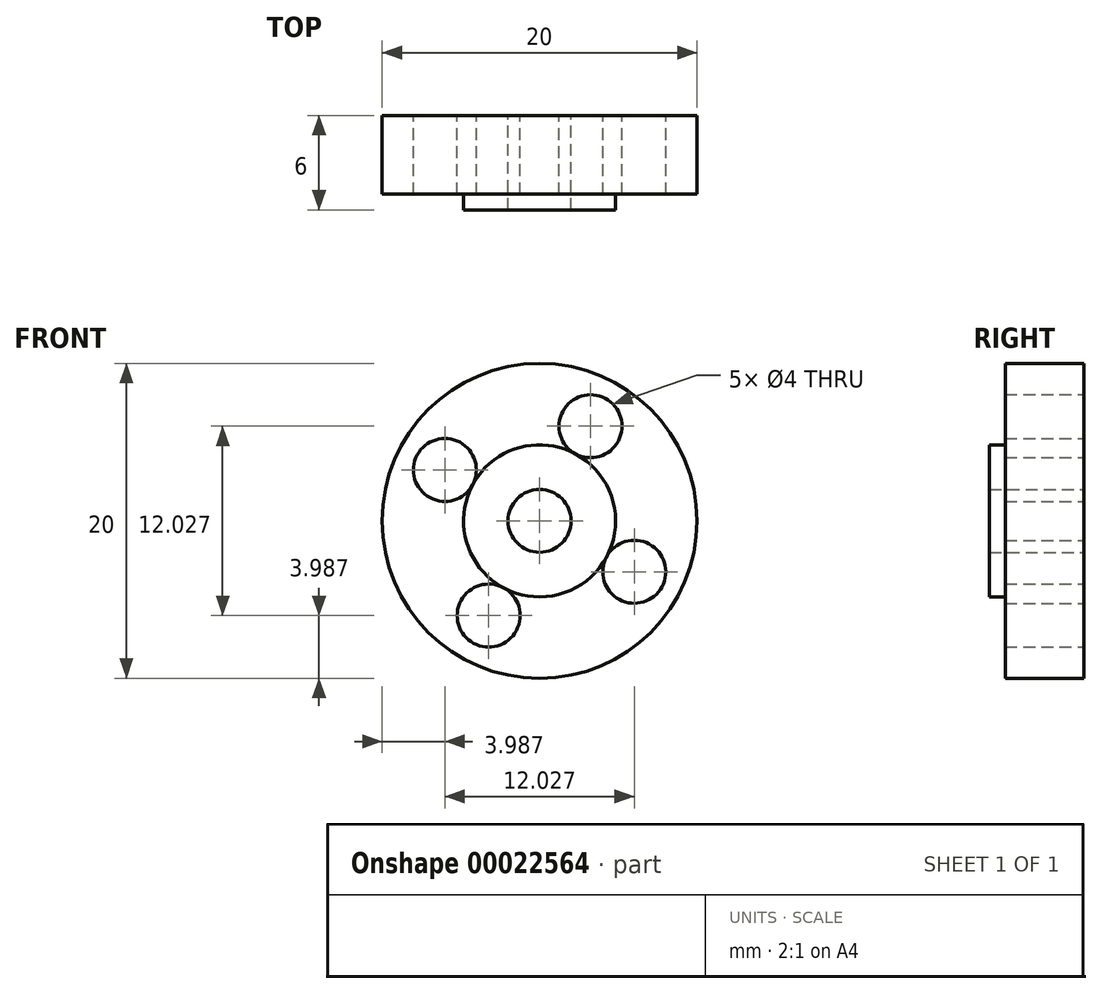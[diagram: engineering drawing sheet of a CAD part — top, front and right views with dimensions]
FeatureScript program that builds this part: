
annotation { "Feature Type Name" : "Feature", "Feature Type Description" : "" }
export const myFeature = defineFeature(function(context is Context, id is Id, definition is map)
    precondition{}
    {
        {
            var Q0;
            Q0=qCreatedBy(makeId("Front.planeOp"),FACE);
            var sketch = newSketch(context, id + "F0", { "sketchPlane" : qUnion([Q0])});
            skCircle(sketch, "E0", {"center": v(0, 0) * mm, "radius": 10 * mm});
            skCircle(sketch, "E1", {"center": v(0, 0) * mm, "radius": 2 * mm});
            skCircle(sketch, "E2", {"center": v(0, 0) * mm, "radius": 4.83 * mm});
            skCircle(sketch, "E3.cCircle", {"center": v(0, 0) * mm, "radius": 4.83 * mm, "construction": true});
            skLineSegment(sketch, "E3.0", {"start": v(6.01, -3.24) * mm, "end": v(-3.24, -6.01) * mm});
            skLineSegment(sketch, "E3.1", {"start": v(-3.24, -6.01) * mm, "end": v(-6.01, 3.24) * mm});
            skLineSegment(sketch, "E3.2", {"start": v(-6.01, 3.24) * mm, "end": v(3.24, 6.01) * mm});
            skLineSegment(sketch, "E3.3", {"start": v(3.24, 6.01) * mm, "end": v(6.01, -3.24) * mm});
            skPoint(sketch, "E3.0.midPoint", {"position": v(1.39, -4.62) * mm});
            skCircle(sketch, "E4", {"center": v(-3.24, -6.01) * mm, "radius": 2 * mm});
            skCircle(sketch, "E5", {"center": v(6.01, -3.24) * mm, "radius": 2 * mm});
            skCircle(sketch, "E6", {"center": v(3.24, 6.01) * mm, "radius": 2 * mm});
            skCircle(sketch, "E7", {"center": v(-6.01, 3.24) * mm, "radius": 2 * mm});
            skSolve(sketch);
        }
        {
            var Q0;
            Q0=makeQuery(id+"F0.imprint","IMPRINT",FACE,{"disambiguationData":[TD([[makeQuery(id+"F0.imprint","IMPRINT",EDGE,{"derivedFrom":sQuery(id+"F0.wireOp",EDGE,"E1")}),-1.0]])]});
            var Q1;
            Q1=makeQuery(id+"F0.imprint","IMPRINT",FACE,{"disambiguationData":[TD([[makeQuery(id+"F0.imprint","IMPRINT",EDGE,{"derivedFrom":sQuery(id+"F0.wireOp",EDGE,"E0")}),1.0]])]});
            var Q2;
            {var subQ0=sQuery(id+"F0.wireOp",EDGE,"E7");var subQ3=sQuery(id+"F0.wireOp",EDGE,"E2");var subQ4=makeQuery(id+"F0.imprint","INTERSECT",VERTEX,{"derivedFrom":[subQ3,subQ0]});Q2=makeQuery(id+"F0.imprint","IMPRINT",FACE,{"disambiguationData":[TD([[makeQuery(id+"F0.imprint","IMPRINT",EDGE,{"disambiguationData":[TD([[subQ4,-1.0]])],"derivedFrom":subQ3}),-1.0]])]});}
            var Q3;
            {var subQ1=sQuery(id+"F0.wireOp",EDGE,"E3.2");var subQ3=sQuery(id+"F0.wireOp",EDGE,"E2");var subQ5=makeQuery(id+"F0.imprint","INTERSECT",VERTEX,{"derivedFrom":[subQ3,subQ1]});Q3=makeQuery(id+"F0.imprint","IMPRINT",FACE,{"disambiguationData":[TD([[makeQuery(id+"F0.imprint","IMPRINT",EDGE,{"disambiguationData":[TD([[subQ5,-1.0]])],"derivedFrom":subQ3}),-1.0]])]});}
            var Q4;
            {var subQ0=sQuery(id+"F0.wireOp",EDGE,"E6");var subQ3=sQuery(id+"F0.wireOp",EDGE,"E2");var subQ4=makeQuery(id+"F0.imprint","INTERSECT",VERTEX,{"derivedFrom":[subQ3,subQ0]});Q4=makeQuery(id+"F0.imprint","IMPRINT",FACE,{"disambiguationData":[TD([[makeQuery(id+"F0.imprint","IMPRINT",EDGE,{"disambiguationData":[TD([[subQ4,-1.0]])],"derivedFrom":subQ3}),-1.0]])]});}
            var Q5;
            {var subQ0=sQuery(id+"F0.wireOp",EDGE,"E6");var subQ3=sQuery(id+"F0.wireOp",EDGE,"E2");var subQ4=makeQuery(id+"F0.imprint","INTERSECT",VERTEX,{"derivedFrom":[subQ3,subQ0]});Q5=makeQuery(id+"F0.imprint","IMPRINT",FACE,{"disambiguationData":[TD([[makeQuery(id+"F0.imprint","IMPRINT",EDGE,{"disambiguationData":[TD([[subQ4,1.0]])],"derivedFrom":subQ3}),-1.0]])]});}
            var Q6;
            {var subQ1=sQuery(id+"F0.wireOp",EDGE,"E3.3");var subQ3=sQuery(id+"F0.wireOp",EDGE,"E2");var subQ5=makeQuery(id+"F0.imprint","INTERSECT",VERTEX,{"derivedFrom":[subQ3,subQ1]});Q6=makeQuery(id+"F0.imprint","IMPRINT",FACE,{"disambiguationData":[TD([[makeQuery(id+"F0.imprint","IMPRINT",EDGE,{"disambiguationData":[TD([[subQ5,1.0]])],"derivedFrom":subQ3}),-1.0]])]});}
            var Q7;
            {var subQ1=sQuery(id+"F0.wireOp",EDGE,"E3.0");var subQ3=sQuery(id+"F0.wireOp",EDGE,"E2");var subQ5=makeQuery(id+"F0.imprint","INTERSECT",VERTEX,{"derivedFrom":[subQ3,subQ1]});Q7=makeQuery(id+"F0.imprint","IMPRINT",FACE,{"disambiguationData":[TD([[makeQuery(id+"F0.imprint","IMPRINT",EDGE,{"disambiguationData":[TD([[subQ5,-1.0]])],"derivedFrom":subQ3}),-1.0]])]});}
            var Q8;
            {var subQ0=sQuery(id+"F0.wireOp",EDGE,"E4");var subQ3=sQuery(id+"F0.wireOp",EDGE,"E2");var subQ4=makeQuery(id+"F0.imprint","INTERSECT",VERTEX,{"derivedFrom":[subQ3,subQ0]});Q8=makeQuery(id+"F0.imprint","IMPRINT",FACE,{"disambiguationData":[TD([[makeQuery(id+"F0.imprint","IMPRINT",EDGE,{"disambiguationData":[TD([[subQ4,-1.0]])],"derivedFrom":subQ3}),-1.0]])]});}
            var Q9;
            {var subQ1=sQuery(id+"F0.wireOp",EDGE,"E3.1");var subQ3=sQuery(id+"F0.wireOp",EDGE,"E2");var subQ5=makeQuery(id+"F0.imprint","INTERSECT",VERTEX,{"derivedFrom":[subQ3,subQ1]});Q9=makeQuery(id+"F0.imprint","IMPRINT",FACE,{"disambiguationData":[TD([[makeQuery(id+"F0.imprint","IMPRINT",EDGE,{"disambiguationData":[TD([[subQ5,-1.0]])],"derivedFrom":subQ3}),-1.0]])]});}
            extrude(context, id + "F1", {"entities" : qUnion([Q0, Q1, Q2, Q3, Q4, Q5, Q6, Q7, Q8, Q9]), "depth" : 5 * mm});
        }
        {
            var Q0;
            Q0=makeQuery(id+"F0.imprint","IMPRINT",FACE,{"disambiguationData":[TD([[makeQuery(id+"F0.imprint","IMPRINT",EDGE,{"derivedFrom":sQuery(id+"F0.wireOp",EDGE,"E1")}),-1.0]])]});
            extrude(context, id + "F2", {"entities" : qUnion([Q0]), "operationType" : NewBodyOperationType.ADD, "depth" : 6 * mm});
        }
    });
